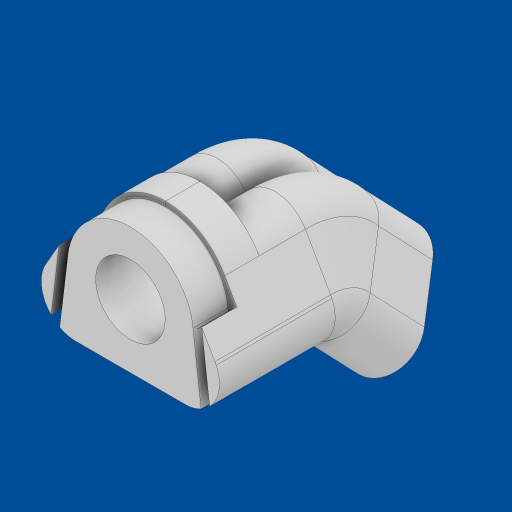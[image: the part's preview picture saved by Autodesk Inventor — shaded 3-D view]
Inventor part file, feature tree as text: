
AUTODESK INVENTOR PART (.ipt)
format: ipt  version: 2023 (Build 270158000, 158)  size: 520,192 bytes
history: native  units: mm
features: extrude x11, sketch x9, plane x3, chamfer x2, mirror x1, revolve x1
ambient origin geometry x8: Origin, YZ Plane, XZ Plane, XY Plane, X Axis, Y Axis, Z Axis, Center Point
bodies: Solid1 (feature_tree)
feature tree (27):
  sketch  "Sketch1"  dims[d0=100.0mm d1=25.0mm d2=7.5mm d3=7.5mm d4=60.0deg d5=15.0mm d6=11.0mm d7=11.0mm d8=15.0mm d14=4.0mm d15=0.0mm]
  extrude  "Extrusion1"  Depth=7.5mm TaperAngle=0.0deg
  plane  "Work Plane13"
  sketch  "Sketch7"  dims[d72=7.5mm d73=90.0deg]
  extrude  "Extrusion6"  TaperAngle=90.0deg  [1 undecoded]
  extrude  "Extrusion7"  Depth=7.5mm
  mirror  "Mirror4"
  plane  "Work Plane9"
  extrude  "Extrusion8"  Depth=15.0mm
  revolve  "Revolution2"  [1 undecoded]
  extrude  "Extrusion9"  Depth=6.5mm
  extrude  "Extrusion10"  Depth=15.0mm TaperAngle=0.0deg
  extrude  "Extrusion11"  Depth=10.0mm TaperAngle=0.0deg
  chamfer  "Chamfer3"  Distance=4.0mm
  chamfer  "Chamfer4"  Distance=10.0mm
  plane  "Work Plane16"
  extrude  "Extrusion14"  Depth=10.0mm TaperAngle=0.0deg
  extrude  "Extrusion21"  Depth=7.55mm TaperAngle=45.0deg
  extrude  "Extrusion23"  Depth=7.55mm TaperAngle=45.0deg
  extrude  "Extrusion25"  Depth=7.55mm
  sketch  "Sketch14"  dims[d74=7.5mm d75=5.5mm]
  sketch  "Sketch15"  dims[d76=5.5mm d77=15.0mm]
  sketch  "Sketch19"  dims[d78=11.0mm d79=11.0mm]
  sketch  "Sketch23"  dims[d80=2.0mm d81=6.5mm]
  sketch  "Sketch24"  dims[d82=6.5mm d83=15.0mm d84=0.0mm]
  sketch  "Sketch33"  dims[d93=10.0mm d94=0.0mm d115=20.0mm d116=0.0mm]
  sketch  "Sketch34"  dims[d131=8.648979mm d132=4.0mm d133=0.0mm d134=10.0mm d135=0.0mm d136=10.0mm d137=0.0mm d138=2.0mm d139=4.0mm d140=45.0deg d141=2.0mm d142=4.0mm d143=45.0deg d153=15.0mm d154=15.0mm d155=15.0mm d156=25.0mm d157=0.0mm d222=45.0mm d243=1.0mm d244=27.222586mm d245=15.0mm d246=0.0mm d255=15.0mm d256=15.0mm d257=0.0mm d266=261.822mm d267=7.45mm d268=27.223mm d269=1.0mm d270=35.0mm d271=100.0mm d272=2.0mm d273=1.1mm d274=180.0deg d275=1.0mm d276=15.709295mm d277=7.55mm d278=0.0mm d279=2.0mm d280=1.0mm d281=180.0deg d182=0.5mm d183=0.872665mm d184=0.5mm d185=0.872665mm d224=0.5mm d225=0.872665mm d226=0.5mm d227=0.872665mm d258=0.5mm d259=0.872665mm d260=0.5mm d261=0.872665mm]
note: 2 required parameter values undecoded (feature->parameter linkage not recoverable at this tier; creation-order binding heuristic only, values carry confidence <= 0.55)